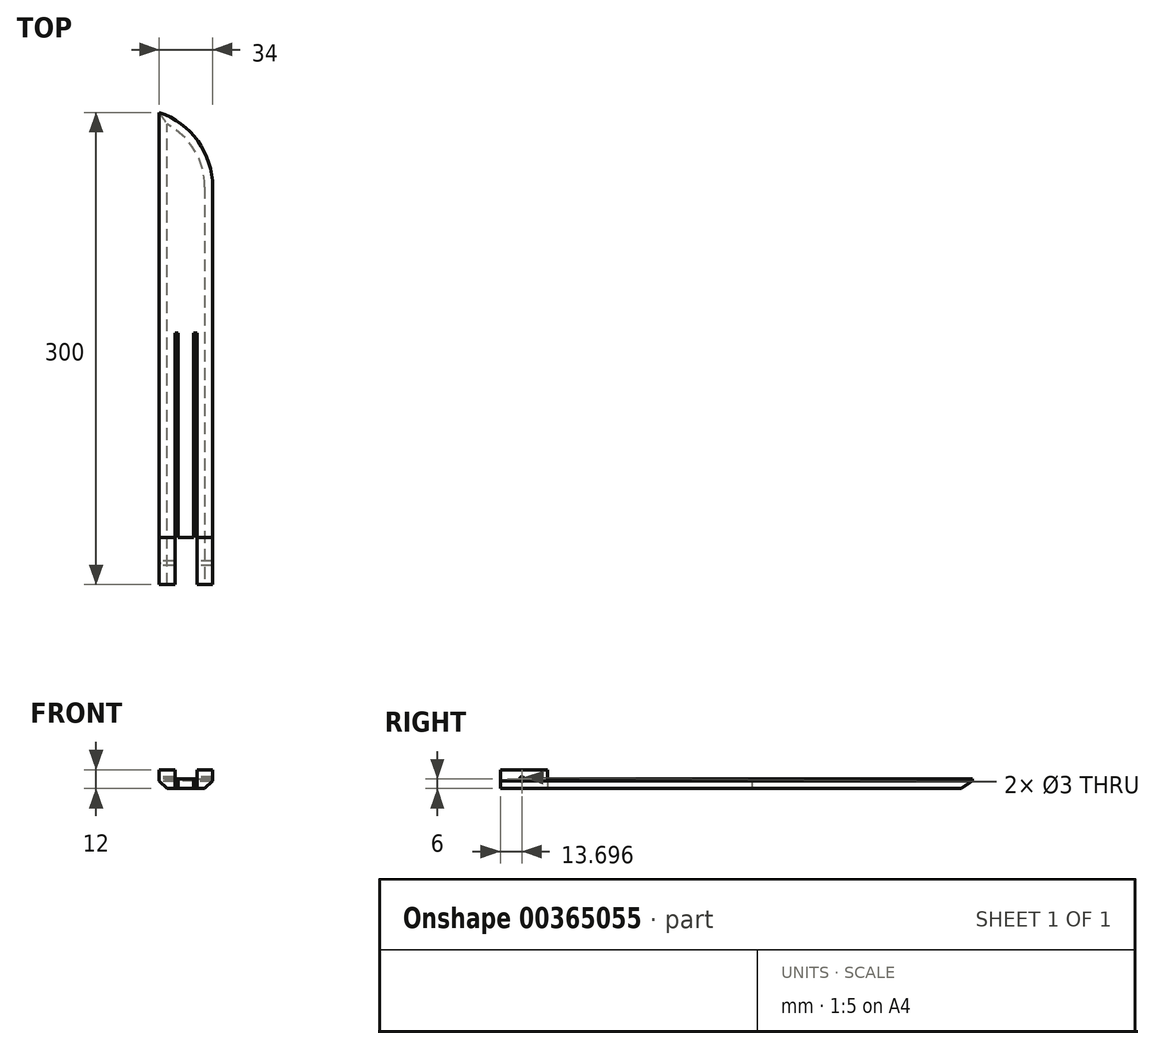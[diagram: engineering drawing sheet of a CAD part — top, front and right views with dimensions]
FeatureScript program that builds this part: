
annotation { "Feature Type Name" : "Feature", "Feature Type Description" : "" }
export const myFeature = defineFeature(function(context is Context, id is Id, definition is map)
    precondition{}
    {
        {
            var Q0;
            Q0=qCreatedBy(makeId("Top.planeOp"),FACE);
            var sketch = newSketch(context, id + "F0", { "sketchPlane" : qUnion([Q0])});
            skLineSegment(sketch, "E0.bottom", {"start": v(17, -150) * mm, "end": v(7, -150) * mm});
            skLineSegment(sketch, "E0.top", {"start": v(17, 150) * mm, "end": v(-17, 150) * mm});
            skLineSegment(sketch, "E0.left", {"start": v(17, -150) * mm, "end": v(17, 150) * mm});
            skLineSegment(sketch, "E0.right", {"start": v(-17, -150) * mm, "end": v(-17, 150) * mm});
            skPoint(sketch, "E0.middle", {"position": v(0, 0) * mm});
            skLineSegment(sketch, "E1.top", {"start": v(-7, 10) * mm, "end": v(-5, 10) * mm});
            skLineSegment(sketch, "E1.left", {"start": v(-7, -150) * mm, "end": v(-7, 10) * mm});
            skLineSegment(sketch, "E1.right", {"start": v(-5, -120) * mm, "end": v(-5, 10) * mm});
            skLineSegment(sketch, "E2.top", {"start": v(5, 10) * mm, "end": v(7, 10) * mm});
            skLineSegment(sketch, "E2.left", {"start": v(5, -120) * mm, "end": v(5, 10) * mm});
            skLineSegment(sketch, "E2.right", {"start": v(7, -150) * mm, "end": v(7, 10) * mm});
            skLineSegment(sketch, "E3.trimOffspring", {"start": v(-7, -150) * mm, "end": v(-17, -150) * mm});
            skLineSegment(sketch, "E4.top", {"start": v(-5, -120) * mm, "end": v(5, -120) * mm});
            skSolve(sketch);
        }
        {
            var Q0;
            Q0=makeQuery(id+"F0.imprint","IMPRINT",FACE,{"disambiguationData":[TD([[makeQuery(id+"F0.imprint","IMPRINT",EDGE,{"derivedFrom":sQuery(id+"F0.wireOp",EDGE,"E0.bottom")}),-1.0]])]});
            extrude(context, id + "F1", {"entities" : qUnion([Q0]), "depth" : 6 * mm});
        }
        {
            var Q0;
            Q0=makeQuery(id+"F1.opExtrude","CAP_FACE",FACE,{"disambiguationData":[OSD([sQuery(id+"F0.wireOp",EDGE,"E0.bottom"),sQuery(id+"F0.wireOp",EDGE,"E0.top"),sQuery(id+"F0.wireOp",EDGE,"E0.left"),sQuery(id+"F0.wireOp",EDGE,"E0.right"),sQuery(id+"F0.wireOp",EDGE,"E1.top"),sQuery(id+"F0.wireOp",EDGE,"E1.left"),sQuery(id+"F0.wireOp",EDGE,"E1.right"),sQuery(id+"F0.wireOp",EDGE,"E2.top"),sQuery(id+"F0.wireOp",EDGE,"E2.left"),sQuery(id+"F0.wireOp",EDGE,"E2.right"),sQuery(id+"F0.wireOp",EDGE,"E3.trimOffspring"),sQuery(id+"F0.wireOp",EDGE,"E4.top")])],"isStart":false});
            var sketch = newSketch(context, id + "F2", { "sketchPlane" : qUnion([Q0])});
            skLineSegment(sketch, "E5.bottom", {"start": v(-7, -120) * mm, "end": v(-17, -120) * mm});
            skLineSegment(sketch, "E5.top", {"start": v(-7, -150) * mm, "end": v(-17, -150) * mm});
            skLineSegment(sketch, "E5.left", {"start": v(-7, -120) * mm, "end": v(-7, -150) * mm});
            skLineSegment(sketch, "E5.right", {"start": v(-17, -120) * mm, "end": v(-17, -150) * mm});
            skLineSegment(sketch, "E6.bottom", {"start": v(7, -120) * mm, "end": v(17, -120) * mm});
            skLineSegment(sketch, "E6.top", {"start": v(7, -150) * mm, "end": v(17, -150) * mm});
            skLineSegment(sketch, "E6.left", {"start": v(7, -120) * mm, "end": v(7, -150) * mm});
            skLineSegment(sketch, "E6.right", {"start": v(17, -120) * mm, "end": v(17, -150) * mm});
            skSolve(sketch);
        }
        {
            var Q0;
            Q0=makeQuery(id+"F2.imprint","IMPRINT",FACE,{"disambiguationData":[TD([[makeQuery(id+"F2.imprint","IMPRINT",EDGE,{"derivedFrom":sQuery(id+"F2.wireOp",EDGE,"E5.bottom")}),1.0]])]});
            var Q1;
            Q1=makeQuery(id+"F2.imprint","IMPRINT",FACE,{"disambiguationData":[TD([[makeQuery(id+"F2.imprint","IMPRINT",EDGE,{"derivedFrom":sQuery(id+"F2.wireOp",EDGE,"E6.bottom")}),-1.0]])]});
            extrude(context, id + "F3", {"entities" : qUnion([Q0, Q1]), "operationType" : NewBodyOperationType.ADD, "depth" : 6 * mm});
        }
        {
            var Q0;
            Q0=makeQuery(id+"F3.boolean.opBoolean","MERGE",FACE,{"derivedFrom":[makeQuery(id+"F1.opExtrude","SWEPT_FACE",FACE,{"disambiguationData":[OSD([sQuery(id+"F0.wireOp",EDGE,"E0.right")])]}),makeQuery(id+"F3.opExtrude","SWEPT_FACE",FACE,{"disambiguationData":[OSD([sQuery(id+"F2.wireOp",EDGE,"E5.right")])]})]});
            var sketch = newSketch(context, id + "F4", { "sketchPlane" : qUnion([Q0])});
            skCircle(sketch, "E7", {"center": v(136.3, 6) * mm, "radius": 1.5 * mm});
            skPoint(sketch, "E7.centerSnap0", {"position": v(150, 6) * mm});
            skSolve(sketch);
        }
        {
            var Q0;
            Q0=makeQuery(id+"F4.imprint","IMPRINT",FACE,{"disambiguationData":[TD([[makeQuery(id+"F4.imprint","IMPRINT",EDGE,{"derivedFrom":sQuery(id+"F4.wireOp",EDGE,"E7")}),1.0]])]});
            extrude(context, id + "F5", {"entities" : qUnion([Q0]), "operationType" : NewBodyOperationType.REMOVE, "endBound" : BoundingType.THROUGH_ALL, "oppositeDirection" : true, "depth" : 25 * mm});
        }
        {
            var Q0;
            Q0=makeQuery(id+"F1.opExtrude","SWEPT_EDGE",EDGE,{"disambiguationData":[OSD([sQuery(id+"F0.wireOp",EDGE,"E0.top"),sQuery(id+"F0.wireOp",EDGE,"E0.left")])]});
            fillet(context, id + "F6", {"entities" : qUnion([Q0]), "radius" : 50 * mm, "tangentPropagation" : true, "allowEdgeOverflow" : false});
        }
        {
            var Q0;
            {var subQ0=sQuery(id+"F0.wireOp",EDGE,"E0.left");var subQ1=sQuery(id+"F0.wireOp",EDGE,"E0.top");Q0=makeQuery(id+"F6.opFillet","BLEND_EDGE",EDGE,{"blendedFrom":[makeQuery(id+"F1.opExtrude","SWEPT_EDGE",EDGE,{"disambiguationData":[OSD([subQ1,subQ0])]}),makeQuery(id+"F1.opExtrude","CAP_FACE",FACE,{"disambiguationData":[OSD([sQuery(id+"F0.wireOp",EDGE,"E0.bottom"),subQ1,subQ0,sQuery(id+"F0.wireOp",EDGE,"E0.right"),sQuery(id+"F0.wireOp",EDGE,"E1.top"),sQuery(id+"F0.wireOp",EDGE,"E1.left"),sQuery(id+"F0.wireOp",EDGE,"E1.right"),sQuery(id+"F0.wireOp",EDGE,"E2.top"),sQuery(id+"F0.wireOp",EDGE,"E2.left"),sQuery(id+"F0.wireOp",EDGE,"E2.right"),sQuery(id+"F0.wireOp",EDGE,"E3.trimOffspring"),sQuery(id+"F0.wireOp",EDGE,"E4.top")])],"isStart":true})],"blendedInto":[makeQuery(id+"F1.opExtrude","CAP_FACE",FACE,{"disambiguationData":[OSD([sQuery(id+"F0.wireOp",EDGE,"E0.bottom"),subQ1,subQ0,sQuery(id+"F0.wireOp",EDGE,"E0.right"),sQuery(id+"F0.wireOp",EDGE,"E1.top"),sQuery(id+"F0.wireOp",EDGE,"E1.left"),sQuery(id+"F0.wireOp",EDGE,"E1.right"),sQuery(id+"F0.wireOp",EDGE,"E2.top"),sQuery(id+"F0.wireOp",EDGE,"E2.left"),sQuery(id+"F0.wireOp",EDGE,"E2.right"),sQuery(id+"F0.wireOp",EDGE,"E3.trimOffspring"),sQuery(id+"F0.wireOp",EDGE,"E4.top")])],"isStart":true})]});}
            var Q1;
            Q1=makeQuery(id+"F1.opExtrude","CAP_EDGE",EDGE,{"disambiguationData":[OSD([sQuery(id+"F0.wireOp",EDGE,"E0.right")])],"isStart":true});
            chamfer(context, id + "F7", {"entities" : qUnion([Q0, Q1]), "width" : 5 * mm, "tangentPropagation" : true});
        }
    });
